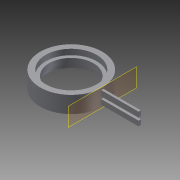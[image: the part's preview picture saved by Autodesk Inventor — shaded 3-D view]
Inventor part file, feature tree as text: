
AUTODESK INVENTOR PART (.ipt)
format: ipt  version: 2012 SP2 (Build 160219200, 219)  size: 134,656 bytes
history: native  units: in
note: dims shown in document units (in); Inventor stores cm internally (conversion verified against a paired STEP export)
features: sketch x3, plane x2, extrude x2, revolve x1, reference x1, projected_geometry x1
ambient origin geometry x8: Origin, YZ Plane, XZ Plane, XY Plane, X Axis, Y Axis, Z Axis, Center Point
bodies: Solid1 (feature_tree)
feature tree (10):
  revolve  "Revolution1"  [1 undecoded]
  plane  "Work Plane1"
  extrude  "Extrusion1"  Depth=0.5906in
  plane  "Work Plane2"
  extrude  "Extrusion2"  Depth=0.1969in
  sketch  "Sketch1"  dims[d0=1.1024in d1=0.7874in]
  sketch  "Sketch2"  dims[d2=0.1181in d3=0.5906in]
  reference  "Reference1"
  sketch  "Sketch3"  dims[d4=10.2362in d5=0.1969in d6=90.0deg d7=0.0197in d8=0.0197in d9=0.1772in d10=0.0787in d11=0.7874in d13=0.2756in d14=0.3937in d16=0.3937in d18=1.3312in d19=0.1031in d20=0.0in d21=0.0in d22=0.2362in d23=0.2953in d24=1.1024in d25=0.2362in d26=0.0in]
  projected_geometry  "Projected Loop1"
note: 1 required parameter value undecoded (feature->parameter linkage not recoverable at this tier; creation-order binding heuristic only, values carry confidence <= 0.55)
